# Revit family: Sanitary_Showers_hansgrohe_25016XXX-RainButton-Symbol-shoulder-show_NEW
name_source: partatom
category: Plumbing Fixtures
revit_build: Autodesk Revit 2018 (Build: 20170223_1515(x64)
units: mm (PartAtom-declared; Revit-internal decimal feet)

## family parameters
Cut with Voids When Loaded = No
Host = Face
OmniClass Number = 23.31.17.00
OmniClass Title = Showers
Part Type = Normal
Room Calculation Point = No
Round Connector Dimension = Use Diameter
Shared = No

## types (6) — shared parameters
Always visible = Yes
BIMobject category = Showers
Date Updated = 12/07/2023
Date of publishing = 11/2/2022 12:00:00 AM
Default Elevation = 1219 mm
Description = RainButton Symbol shoulder shower
Design country = Germany
EAN code = 4059625284247
Edition number = 1
IFC Classification = Sanitary Terminal
Manufacturer = Hansgrohe
Manufacturer country = Germany
Manufacturer name = hansgrohe
Masterformat 2014 Code = 22 41 23
Masterformat 2014 Description = Residential Showers
Model = 25016XXX
OmniClass Code = 23-31 17 00
OmniClass Description = Showers
Product Guid = bbfa2ced-ed78-4c81-8387-4dcfb38e760d
Product SKU = 25016XXX
Product data url = https://bimobject.com
Product family = Electronic controllers
Product group = RainButton
Product name = 25016XXX RainButton Symbol shoulder shower
Product url = https://pro.hansgrohe.com
QR code = https://bimobject.com
UNSPSC Code = 30181503
URL = https://www.hansgrohe.com
Uniclass 2015 Code = Pr_40_20_87_76
Uniclass 2015 Name = Shower heads
Uniformat II Code = D2010
Uniformat II Description = Plumbing Fixtures
Version = 2
Weight Net (Kg) = 140

## per-type parameters (varying)
| type | Material | Material 1 |
| 000 Chrome | Hansgrohe - Metal - 000 Chrome | Hansgrohe - Glass - 000 Symbol shoulder shower |
| 140 Brushed Bronze | Hansgrohe - Metal - 140 Brushed Bronze | Hansgrohe - Glass - Symbol shoulder shower |
| 340 Brushed Black Chrome | Hansgrohe - Metal - 340 Brushed Black Chrome | Hansgrohe - Glass - Symbol shoulder shower |
| 670 Matte Black | Hansgrohe - Metal - 670 Matte Black | Hansgrohe - Glass - Symbol shoulder shower |
| 700 Matte White | Hansgrohe - Metal - 700 Matte White | Hansgrohe - Glass - Symbol shoulder shower |
| 990 Polished Gold Optic | Hansgrohe - Metal - 990 Polished Gold Optic | Hansgrohe - Glass - Symbol shoulder shower |

## geometry (parser evidence)
native form markers: Sweep x2
no freeform markers — native parametric forms only
